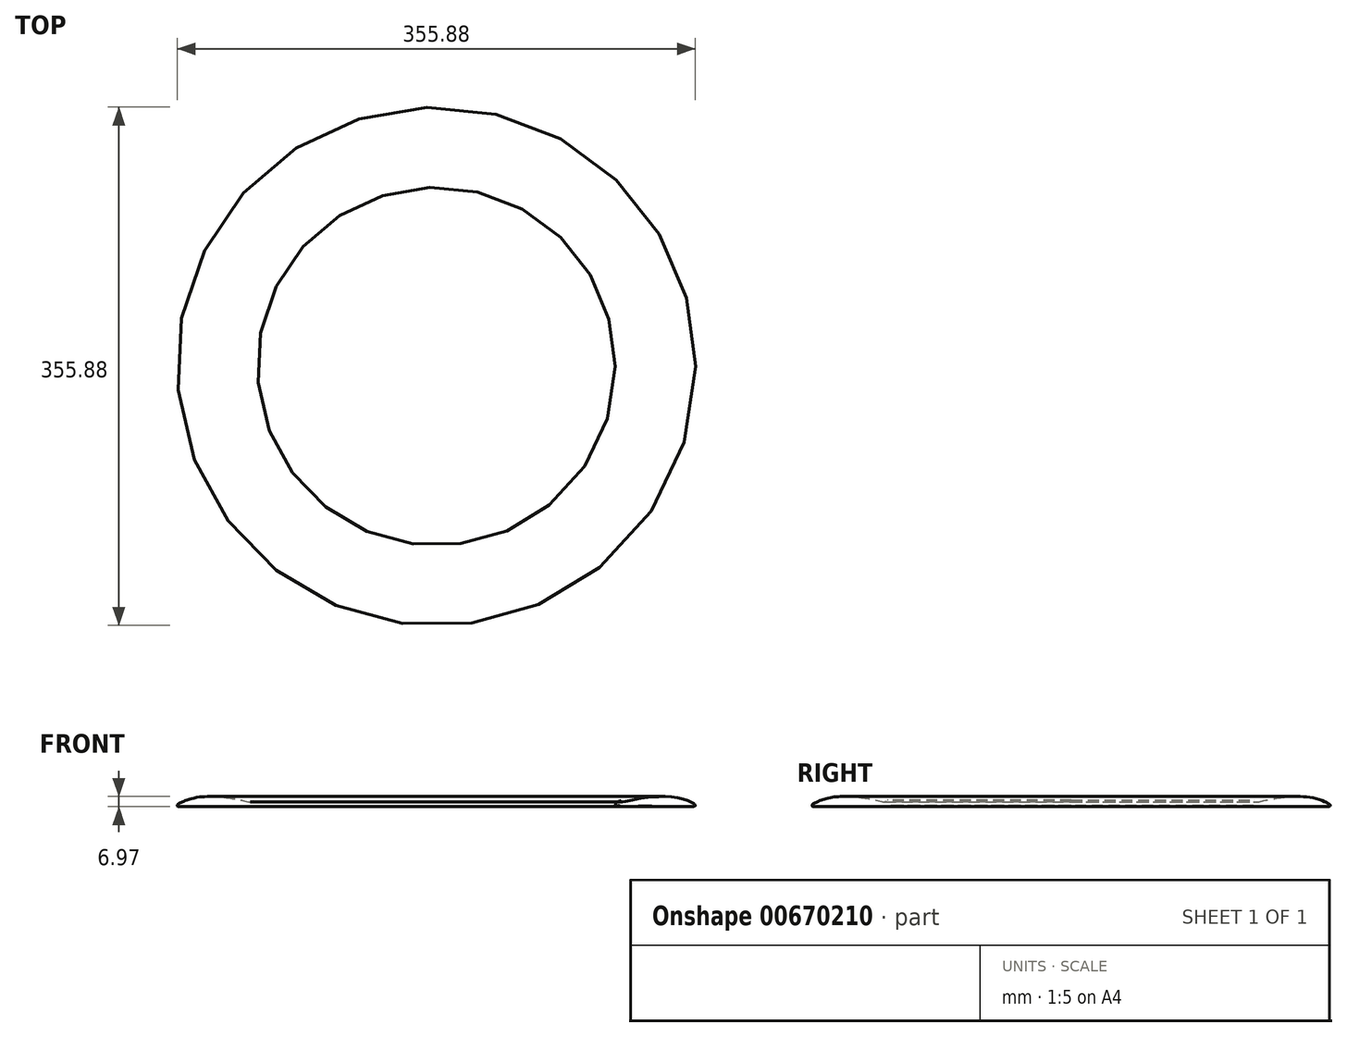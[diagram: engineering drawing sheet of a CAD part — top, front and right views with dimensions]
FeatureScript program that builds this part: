
annotation { "Feature Type Name" : "Feature", "Feature Type Description" : "" }
export const myFeature = defineFeature(function(context is Context, id is Id, definition is map)
    precondition{}
    {
        {
            var Q0;
            Q0=qCreatedBy(makeId("Front.planeOp"),FACE);
            var sketch = newSketch(context, id + "F0", { "sketchPlane" : qUnion([Q0])});
            skFitSpline(sketch, "E0", {"points": [v(1.76, 7.2) * mm, v(2.87, 5.96) * mm, v(7.03, 6.38) * mm, v(21.16, 8.87) * mm, v(27.4, 9.29) * mm, v(36.4, 9.36) * mm, v(44.86, 7.83) * mm, v(49.71, 6.1) * mm, v(52.34, 4.78) * mm, v(53.73, 3.81) * mm, v(53.8, 2.98) * mm, v(52.41, 2.5) * mm, v(50.82, 2.63) * mm, v(45.7, 2.57) * mm, v(10.29, 2.77) * mm, v(2.73, 2.7) * mm, v(1.14, 3.26) * mm, v(0, 2.77) * mm, v(-1.15, 3.26) * mm, v(1.76, 7.2) * mm]});
            skLineSegment(sketch, "E1", {"start": v(-124.04, 23.66) * mm, "end": v(-124.04, -26.53) * mm});
            skSolve(sketch);
        }
        {
            var Q0;
            Q0=makeQuery(id+"F0.imprint","IMPRINT",FACE,{"disambiguationData":[TD([[makeQuery(id+"F0.imprint","IMPRINT",EDGE,{"derivedFrom":sQuery(id+"F0.wireOp",EDGE,"E0")}),-1.0]])]});
            var Q1;
            Q1=sQuery(id+"F0.wireOp",EDGE,"E1");
            revolve(context, id + "F1", {"entities" : qUnion([Q0]), "axis" : qUnion([Q1]), "revolveType" : RevolveType.FULL});
        }
    });
